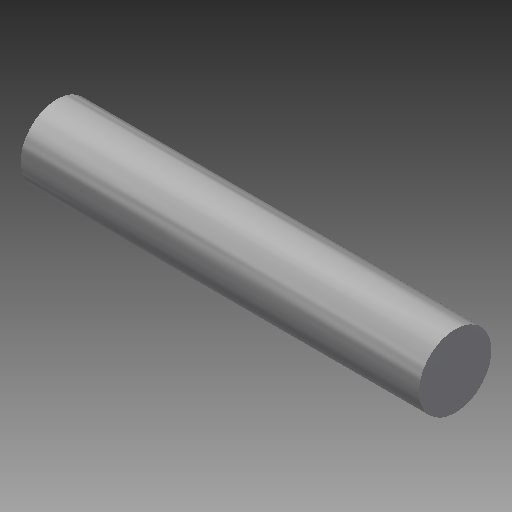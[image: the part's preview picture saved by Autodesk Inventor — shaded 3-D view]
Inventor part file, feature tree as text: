
AUTODESK INVENTOR PART (.ipt)
format: ipt  version: 2017 SP1 (Build 210196100, 196)  size: 97,792 bytes
history: native  units: mm
features: other x3, revolve x1
ambient origin geometry x6: Origin, XZ Plane, XY Plane, X Axis, Y Axis, Z Axis
bodies: Solid1 (feature_tree)
feature tree (4):
  revolve  "Revolution1"  [1 undecoded]
  other  "Start Plane"
  other  "Origin point"
  other  "Main Sketch"
note: 1 required parameter value undecoded (feature->parameter linkage not recoverable at this tier; creation-order binding heuristic only, values carry confidence <= 0.55)
